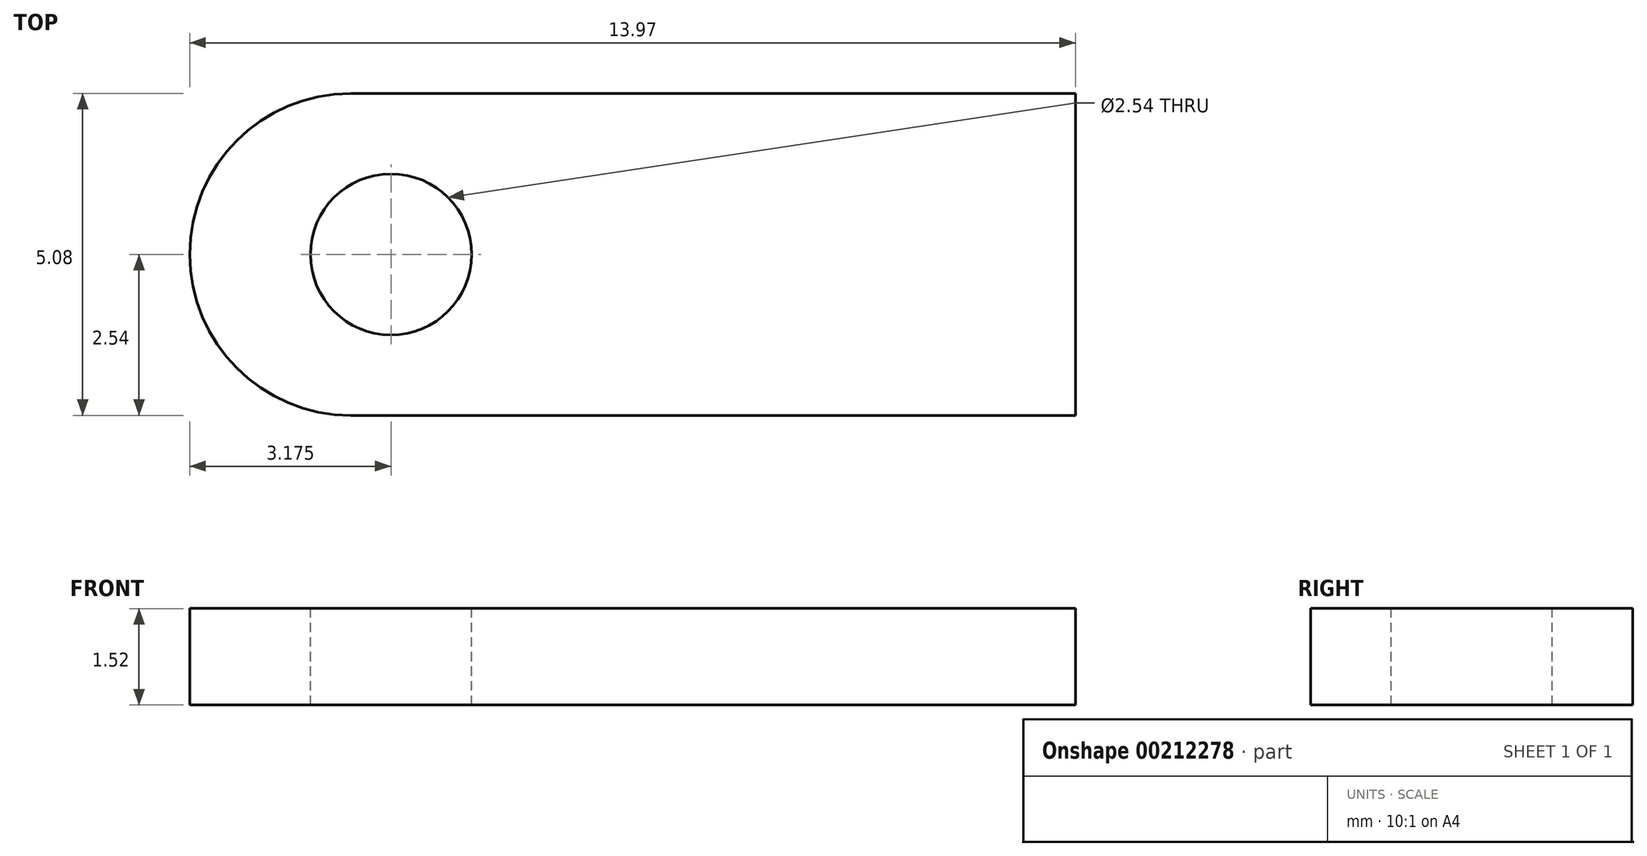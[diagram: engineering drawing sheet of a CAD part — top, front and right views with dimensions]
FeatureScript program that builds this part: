
annotation { "Feature Type Name" : "Feature", "Feature Type Description" : "" }
export const myFeature = defineFeature(function(context is Context, id is Id, definition is map)
    precondition{}
    {
        {
            var Q0;
            Q0=qCreatedBy(makeId("Top.planeOp"),FACE);
            var sketch = newSketch(context, id + "F0", { "sketchPlane" : qUnion([Q0])});
            skLineSegment(sketch, "E0.bottom", {"start": v(0, 0) * mm, "end": v(13.97, 0) * mm});
            skLineSegment(sketch, "E0.top", {"start": v(0, 5.08) * mm, "end": v(13.97, 5.08) * mm});
            skLineSegment(sketch, "E0.left", {"start": v(0, 0) * mm, "end": v(0, 5.08) * mm});
            skLineSegment(sketch, "E0.right", {"start": v(13.97, 0) * mm, "end": v(13.97, 5.08) * mm});
            skSolve(sketch);
        }
        {
            var Q0;
            Q0=makeQuery(id+"F0.imprint","IMPRINT",FACE,{"disambiguationData":[TD([[makeQuery(id+"F0.imprint","IMPRINT",EDGE,{"derivedFrom":sQuery(id+"F0.wireOp",EDGE,"E0.bottom")}),1.0]])]});
            extrude(context, id + "F1", {"entities" : qUnion([Q0]), "depth" : 1.52 * mm});
        }
        {
            var Q0;
            Q0=makeQuery(id+"F1.opExtrude","CAP_FACE",FACE,{"disambiguationData":[OSD([sQuery(id+"F0.wireOp",EDGE,"E0.bottom"),sQuery(id+"F0.wireOp",EDGE,"E0.top"),sQuery(id+"F0.wireOp",EDGE,"E0.left"),sQuery(id+"F0.wireOp",EDGE,"E0.right")])],"isStart":false});
            var sketch = newSketch(context, id + "F2", { "sketchPlane" : qUnion([Q0])});
            skCircle(sketch, "E1", {"center": v(3.18, 2.54) * mm, "radius": 1.27 * mm});
            skSolve(sketch);
        }
        {
            var Q0;
            Q0=makeQuery(id+"F2.imprint","IMPRINT",FACE,{"disambiguationData":[TD([[makeQuery(id+"F2.imprint","IMPRINT",EDGE,{"derivedFrom":sQuery(id+"F2.wireOp",EDGE,"E1")}),1.0]])]});
            extrude(context, id + "F3", {"entities" : qUnion([Q0]), "operationType" : NewBodyOperationType.REMOVE, "oppositeDirection" : true, "depth" : 25.4 * mm});
        }
        {
            var Q0;
            Q0=makeQuery(id+"F1.opExtrude","SWEPT_EDGE",EDGE,{"disambiguationData":[OSD([sQuery(id+"F0.wireOp",EDGE,"E0.bottom"),sQuery(id+"F0.wireOp",EDGE,"E0.left")])]});
            var Q1;
            Q1=makeQuery(id+"F1.opExtrude","SWEPT_EDGE",EDGE,{"disambiguationData":[OSD([sQuery(id+"F0.wireOp",EDGE,"E0.top"),sQuery(id+"F0.wireOp",EDGE,"E0.left")])]});
            fillet(context, id + "F4", {"entities" : qUnion([Q0, Q1]), "radius" : 2.54 * mm, "tangentPropagation" : true, "allowEdgeOverflow" : false});
        }
    });
